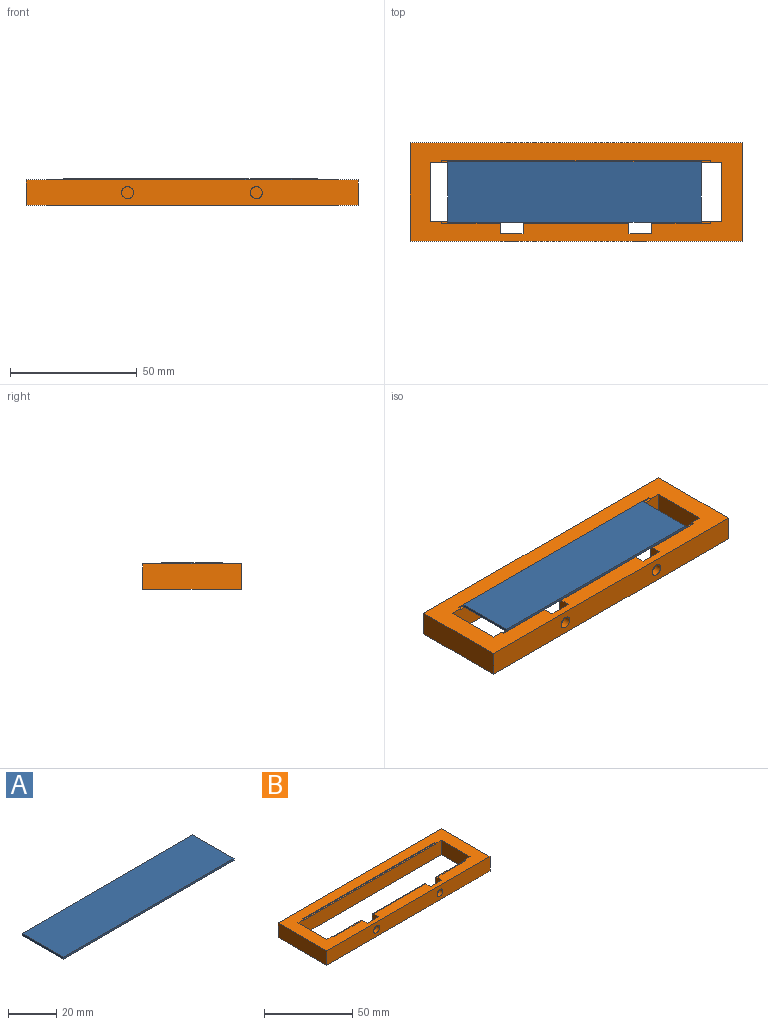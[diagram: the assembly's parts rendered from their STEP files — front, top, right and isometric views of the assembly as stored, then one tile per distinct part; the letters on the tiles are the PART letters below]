
ASSEMBLY  parts=2 mates=1
PART A: 6 faces, bbox 100x24x1 mm
  f0: plane 100x1mm, normal (0,-1,0), area 100mm2, adj f1,f3,f4,f5
  f1: plane 24x1mm, normal (1,0,0), area 24mm2, adj f0,f2,f4,f5
  f2: plane 100x1mm, normal (0,1,0), area 100mm2, adj f1,f3,f4,f5
  f3: plane 24x1mm, normal (-1,0,0), area 24mm2, adj f0,f2,f4,f5
  f4: plane 100x24mm, normal (0,0,1), area 2400mm2, adj f0,f1,f2,f3
  f5: plane 100x24mm, normal (0,0,-1), area 2400mm2, adj f0,f1,f2,f3
PART B: 32 faces, bbox 131x39x10 mm
  f0: plane 115x10mm, normal (0,-1,0), area 1097mm2, adj f7,f11,f15,f17,f19,f20,f21
  f1: plane 10x5mm, normal (-1,0,0), area 49.5mm2, adj f7,f12,f13,f17,f27,f28
  f2: plane 10x5mm, normal (1,0,0), area 49.5mm2, adj f3,f7,f13,f17,f25,f26
  f3: plane 41.8x9.5mm, normal (0,1,0), area 397.1mm2, adj f2,f4,f17,f25
  f4: plane 10x5mm, normal (-1,0,0), area 49.5mm2, adj f3,f7,f14,f17,f25,f26
  f5: plane 10x5mm, normal (1,0,0), area 49.5mm2, adj f6,f7,f14,f17,f22,f24
  f6: plane 27.6x10mm, normal (0,1,0), area 264.5mm2, adj f5,f7,f15,f17,f22,f23
  f7: plane 131x39mm, normal (0,0,1), area 2180mm2, adj f0,f1,f2,f4,f5,f6,f8,f9
  f8: plane 131x10mm, normal (0,1,0), area 1310mm2, adj f7,f9,f16,f17
  f9: plane 39x10mm, normal (-1,0,0), area 390mm2, adj f7,f8,f10,f17
  f10: plane 131x10mm, normal (0,-1,0), area 1274.6mm2, adj f7,f9,f16,f17,f30,f31
  f11: plane 23x10mm, normal (-1,0,0), area 230mm2, adj f0,f7,f12,f17
  f12: plane 27.6x10mm, normal (0,1,0), area 264.5mm2, adj f1,f7,f11,f17,f27,f29
  f13: plane 10x9mm, normal (0,1,0), area 72.3mm2, adj f1,f2,f7,f17,f31
  f14: plane 10x9mm, normal (0,1,0), area 72.3mm2, adj f4,f5,f7,f17,f30
  f15: plane 23x10mm, normal (1,0,0), area 230mm2, adj f0,f6,f7,f17
  f16: plane 39x10mm, normal (1,0,0), area 390mm2, adj f7,f8,f10,f17
  f17: plane 131x39mm, normal (0,0,-1), area 2374mm2, adj f0,f1,f2,f3,f4,f5,f6,f8
  f18: plane 106x0.5mm, normal (0,-1,0), area 53mm2, adj f7,f19,f20,f21
  f19: plane 106x1mm, normal (0,0,1), area 106mm2, adj f0,f18,f20,f21
  f20: plane 1x0.5mm, normal (-1,0,0), area 0.5mm2, adj f0,f7,f18,f19
  f21: plane 1x0.5mm, normal (1,0,0), area 0.5mm2, adj f0,f7,f18,f19
  f22: plane 23.1x1mm, normal (0,0,1), area 23.1mm2, adj f5,f6,f23,f24
  f23: plane 1x0.5mm, normal (1,0,0), area 0.5mm2, adj f6,f7,f22,f24
  f24: plane 23.1x0.5mm, normal (0,1,0), area 11.6mm2, adj f5,f7,f22,f23
  f25: plane 41.8x1mm, normal (0,0,1), area 41.8mm2, adj f2,f3,f4,f26
  f26: plane 41.8x0.5mm, normal (0,1,0), area 20.9mm2, adj f2,f4,f7,f25
  f27: plane 23.1x1mm, normal (0,0,1), area 23.1mm2, adj f1,f12,f28,f29
  f28: plane 23.1x0.5mm, normal (0,1,0), area 11.6mm2, adj f1,f7,f27,f29
  f29: plane 1x0.5mm, normal (-1,0,0), area 0.5mm2, adj f7,f12,f27,f28
  f30: cylinder r=2.38mm len=4.75mm, axis (0,-1,0), area 44.8mm2, adj f10,f14
  f31: cylinder r=2.38mm len=4.75mm, axis (0,-1,0), area 44.8mm2, adj f10,f13
PLACE A t=(12.32,28.52,40.05)mm
PLACE B t=(12.95,28.5,30.55)mm fixed
MATE planar B.f19 <-> A.f5  axis (0,0,1) through (12.95,41,40.05)mm
